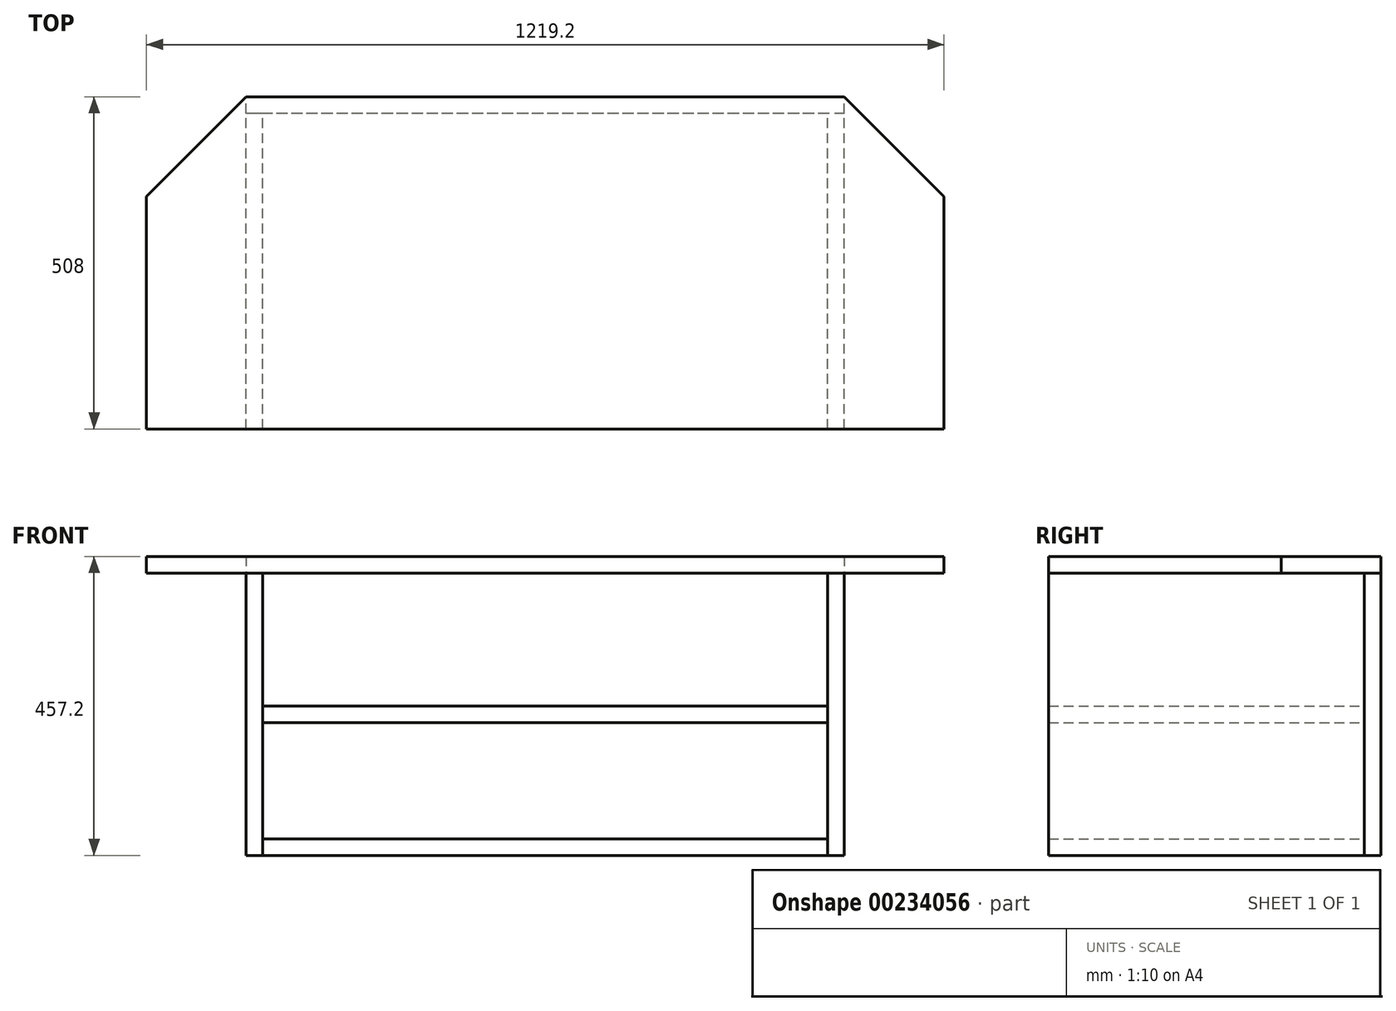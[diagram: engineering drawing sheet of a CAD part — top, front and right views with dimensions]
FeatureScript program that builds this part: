
annotation { "Feature Type Name" : "Feature", "Feature Type Description" : "" }
export const myFeature = defineFeature(function(context is Context, id is Id, definition is map)
    precondition{}
    {
        {
            var Q0;
            Q0=qCreatedBy(makeId("Top.planeOp"),FACE);
            var sketch = newSketch(context, id + "F0", { "sketchPlane" : qUnion([Q0])});
            skLineSegment(sketch, "E0.bottom", {"start": v(457.2, 254) * mm, "end": v(-457.2, 254) * mm});
            skLineSegment(sketch, "E0.top", {"start": v(609.6, -254) * mm, "end": v(-609.6, -254) * mm});
            skLineSegment(sketch, "E0.left", {"start": v(609.6, 101.6) * mm, "end": v(609.6, -254) * mm});
            skLineSegment(sketch, "E0.right", {"start": v(-609.6, 101.6) * mm, "end": v(-609.6, -254) * mm});
            skPoint(sketch, "E0.middle", {"position": v(0, 0) * mm});
            skLineSegment(sketch, "E1", {"start": v(-609.6, 101.6) * mm, "end": v(-457.2, 254) * mm});
            skLineSegment(sketch, "E2", {"start": v(457.2, 254) * mm, "end": v(609.6, 101.6) * mm});
            skLineSegment(sketch, "E3", {"start": v(-609.6, 101.6) * mm, "end": v(609.6, 101.6) * mm, "construction": true});
            skPoint(sketch, "E4.orphan", {"position": v(-609.6, 254) * mm});
            skPoint(sketch, "E5.orphan", {"position": v(609.6, 254) * mm});
            skSolve(sketch);
        }
        {
            var Q0;
            Q0 = qSketchRegion(id + "F0", true);
            extrude(context, id + "F1", {"entities" : qUnion([Q0]), "depth" : 25.4 * mm});
        }
        {
            var Q0;
            Q0=makeQuery(id+"F1.opExtrude","SWEPT_FACE",FACE,{"disambiguationData":[OSD([sQuery(id+"F0.wireOp",EDGE,"E0.bottom")])]});
            var sketch = newSketch(context, id + "F2", { "sketchPlane" : qUnion([Q0])});
            skLineSegment(sketch, "E6", {"start": v(-457.2, 0) * mm, "end": v(-457.2, -431.8) * mm});
            skLineSegment(sketch, "E7", {"start": v(-457.2, -431.8) * mm, "end": v(457.2, -431.8) * mm});
            skLineSegment(sketch, "E8", {"start": v(457.2, -431.8) * mm, "end": v(457.2, 0) * mm});
            skLineSegment(sketch, "E9", {"start": v(457.2, 0) * mm, "end": v(-457.2, 0) * mm});
            skLineSegment(sketch, "E10", {"start": v(-431.8, 0) * mm, "end": v(-431.8, -431.8) * mm});
            skLineSegment(sketch, "E11", {"start": v(431.8, 0) * mm, "end": v(431.8, -431.8) * mm});
            skLineSegment(sketch, "E12", {"start": v(-431.8, -203.2) * mm, "end": v(431.8, -203.2) * mm});
            skPoint(sketch, "E12.endSnap0", {"position": v(431.8, -215.9) * mm});
            skLineSegment(sketch, "E13", {"start": v(431.8, -228.6) * mm, "end": v(-431.8, -228.6) * mm});
            skLineSegment(sketch, "E14", {"start": v(-431.8, -215.9) * mm, "end": v(431.8, -215.9) * mm, "construction": true});
            skLineSegment(sketch, "E15", {"start": v(-431.8, -406.4) * mm, "end": v(431.8, -406.4) * mm});
            skSolve(sketch);
        }
        {
            var Q0;
            {var subQ1=sQuery(id+"F2.wireOp",EDGE,"E6");Q0=makeQuery(id+"F2.imprint","IMPRINT",FACE,{"disambiguationData":[TD([[makeQuery(id+"F2.imprint","IMPRINT",EDGE,{"derivedFrom":subQ1}),1.0]])]});}
            var Q1;
            {var subQ1=sQuery(id+"F2.wireOp",EDGE,"E8");Q1=makeQuery(id+"F2.imprint","IMPRINT",FACE,{"disambiguationData":[TD([[makeQuery(id+"F2.imprint","IMPRINT",EDGE,{"derivedFrom":subQ1}),1.0]])]});}
            var Q2;
            Q2=makeQuery(id+"F1.opExtrude","SWEPT_FACE",FACE,{"disambiguationData":[OSD([sQuery(id+"F0.wireOp",EDGE,"E0.top")])]});
            extrude(context, id + "F3", {"entities" : qUnion([Q0, Q1]), "endBound" : BoundingType.UP_TO_SURFACE, "oppositeDirection" : true, "endBoundEntityFace" : qUnion([Q2]), "depth" : 25.4 * mm, "hasSecondDirection" : true, "secondDirectionOppositeDirection" : true, "secondDirectionDepth" : 25.4 * mm});
        }
        {
            var Q0;
            {var subQ0=sQuery(id+"F2.wireOp",EDGE,"E12");Q0=makeQuery(id+"F2.imprint","IMPRINT",FACE,{"disambiguationData":[TD([[makeQuery(id+"F2.imprint","IMPRINT",EDGE,{"derivedFrom":subQ0}),-1.0]])]});}
            var Q1;
            {var subQ5=sQuery(id+"F2.wireOp",EDGE,"E15");Q1=makeQuery(id+"F2.imprint","IMPRINT",FACE,{"disambiguationData":[TD([[makeQuery(id+"F2.imprint","IMPRINT",EDGE,{"derivedFrom":subQ5}),-1.0]])]});}
            var Q2;
            Q2=makeQuery(id+"F1.opExtrude","SWEPT_FACE",FACE,{"disambiguationData":[OSD([sQuery(id+"F0.wireOp",EDGE,"E0.top")])]});
            extrude(context, id + "F4", {"entities" : qUnion([Q0, Q1]), "endBound" : BoundingType.UP_TO_SURFACE, "oppositeDirection" : true, "endBoundEntityFace" : qUnion([Q2]), "depth" : 25.4 * mm, "hasSecondDirection" : true, "secondDirectionOppositeDirection" : true, "secondDirectionDepth" : 25.4 * mm});
        }
        {
            var Q0;
            Q0=makeQuery(id+"F3.boolean.opBoolean","MERGE",FACE,{"derivedFrom":[makeQuery(id+"F1.opExtrude","SWEPT_FACE",FACE,{"disambiguationData":[OSD([sQuery(id+"F0.wireOp",EDGE,"E0.bottom")])]}),makeQuery(id+"F3.opExtrude","CAP_FACE",FACE,{"disambiguationData":[OSD([sQuery(id+"F2.wireOp",EDGE,"E6"),sQuery(id+"F2.wireOp",EDGE,"E7"),sQuery(id+"F2.wireOp",EDGE,"E8"),sQuery(id+"F2.wireOp",EDGE,"E9"),sQuery(id+"F2.wireOp",EDGE,"E10"),sQuery(id+"F2.wireOp",EDGE,"E11"),sQuery(id+"F2.wireOp",EDGE,"E12"),sQuery(id+"F2.wireOp",EDGE,"E13"),sQuery(id+"F2.wireOp",EDGE,"E15")])],"isStart":true})]});
            var sketch = newSketch(context, id + "F5", { "sketchPlane" : qUnion([Q0])});
            skLineSegment(sketch, "E16.bottom", {"start": v(-457.2, 0) * mm, "end": v(457.2, 0) * mm});
            skLineSegment(sketch, "E16.top", {"start": v(-457.2, -431.8) * mm, "end": v(457.2, -431.8) * mm});
            skLineSegment(sketch, "E16.left", {"start": v(-457.2, 0) * mm, "end": v(-457.2, -431.8) * mm});
            skLineSegment(sketch, "E16.right", {"start": v(457.2, 0) * mm, "end": v(457.2, -431.8) * mm});
            skSolve(sketch);
        }
        {
            var Q0;
            Q0 = qSketchRegion(id + "F5", true);
            extrude(context, id + "F6", {"entities" : qUnion([Q0]), "oppositeDirection" : true, "depth" : 25.4 * mm});
        }
    });
